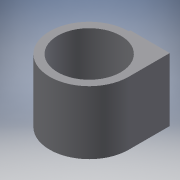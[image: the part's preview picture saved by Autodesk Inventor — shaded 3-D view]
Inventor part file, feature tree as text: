
AUTODESK INVENTOR PART (.ipt)
format: ipt  version: 2016 (Build 200138000, 138)  size: 119,296 bytes
history: native  units: in
note: dims shown in document units (in); Inventor stores cm internally (conversion verified against a paired STEP export)
features: extrude x3, sketch x3
ambient origin geometry x8: Origin, YZ Plane, XZ Plane, XY Plane, X Axis, Y Axis, Z Axis, Center Point
bodies: Solid1 (feature_tree)
feature tree (6):
  extrude  "Extrusion1"  Depth=1.25in
  extrude  "Extrusion2"  Depth=1.0in TaperAngle=0.0deg
  extrude  "Extrusion3"  Depth=0.3125in
  sketch  "Sketch1"  dims[d0=1.0in d1=1.25in]
  sketch  "Sketch2"  dims[d2=0.15in d3=1.0in d4=0.0in]
  sketch  "Sketch3"  dims[d5=0.2in d6=0.3125in d7=0.515in d8=0.0in d9=0.25in d10=0.3125in d11=0.2in d12=0.0in]
